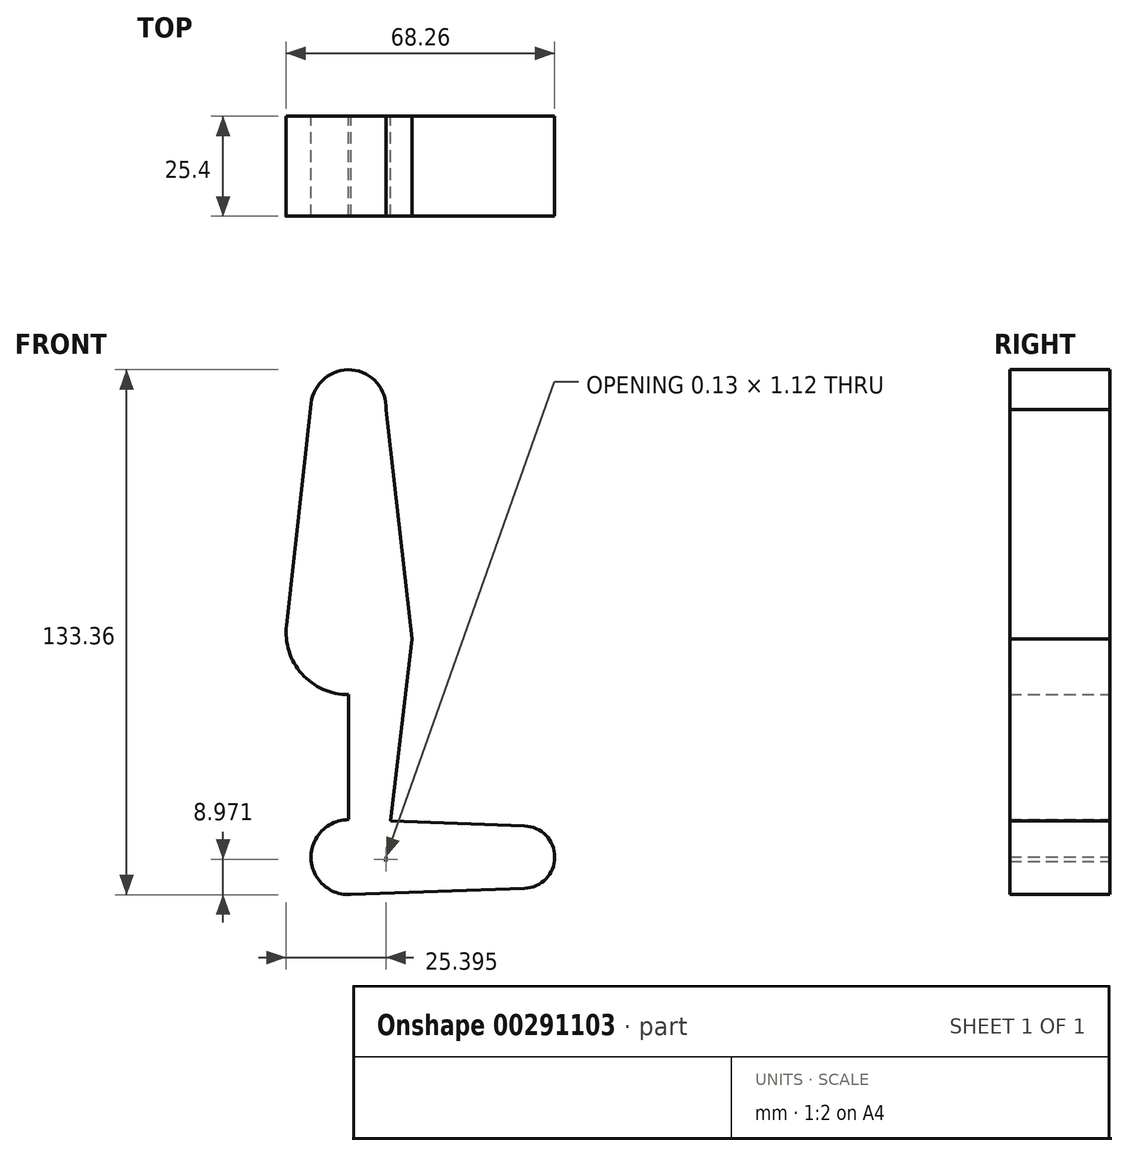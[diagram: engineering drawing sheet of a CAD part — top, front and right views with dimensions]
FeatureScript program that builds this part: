
annotation { "Feature Type Name" : "Feature", "Feature Type Description" : "" }
export const myFeature = defineFeature(function(context is Context, id is Id, definition is map)
    precondition{}
    {
        {
            var Q0;
            Q0=qCreatedBy(makeId("Front.planeOp"),FACE);
            var sketch = newSketch(context, id + "F0", { "sketchPlane" : qUnion([Q0])});
            skPoint(sketch, "E0.middle", {"position": v(0, 0) * mm});
            skPoint(sketch, "E1.end.orphan", {"position": v(0, 114.3) * mm});
            skCircle(sketch, "E2", {"center": v(0, 0) * mm, "radius": 9.53 * mm});
            skCircle(sketch, "E3", {"center": v(44.45, 0) * mm, "radius": 7.94 * mm});
            skPoint(sketch, "E4.center.orphan", {"position": v(0, 57.15) * mm});
            skCircle(sketch, "E5", {"center": v(0, 114.3) * mm, "radius": 9.53 * mm});
            skCircle(sketch, "E6", {"center": v(0, 57.15) * mm, "radius": 15.88 * mm});
            skLineSegment(sketch, "E7", {"start": v(0, 0) * mm, "end": v(44.45, 0) * mm});
            skLineSegment(sketch, "E8", {"start": v(0, 114.3) * mm, "end": v(0, 0) * mm});
            skLineSegment(sketch, "E9", {"start": v(9.6, 0) * mm, "end": v(9.46, -1.12) * mm});
            skPoint(sketch, "E10.orphan", {"position": v(-9.58, 0) * mm});
            skLineSegment(sketch, "E11", {"start": v(-9.48, 115.27) * mm, "end": v(-16.16, 55.46) * mm});
            skLineSegment(sketch, "E12", {"start": v(9.5, 113.67) * mm, "end": v(16.17, 55.46) * mm});
            skLineSegment(sketch, "E13", {"start": v(16.17, 55.46) * mm, "end": v(9.6, 0) * mm});
            skLineSegment(sketch, "E14", {"start": v(0, 9.53) * mm, "end": v(44.73, 7.93) * mm});
            skLineSegment(sketch, "E15", {"start": v(0, -9.52) * mm, "end": v(44.73, -7.93) * mm});
            skLineSegment(sketch, "E16", {"start": v(-16.16, 55.46) * mm, "end": v(-9.58, 0) * mm});
            skSolve(sketch);
        }
        {
            var Q0;
            Q0 = qSketchRegion(id + "F0", true);
            extrude(context, id + "F1", {"entities" : qUnion([Q0]), "depth" : 25.4 * mm});
        }
        {
            var Q0;
            Q0 = qSketchRegion(id + "F0", true);
            extrude(context, id + "F2", {"entities" : qUnion([Q0]), "operationType" : NewBodyOperationType.ADD, "depth" : 25.4 * mm});
        }
    });
